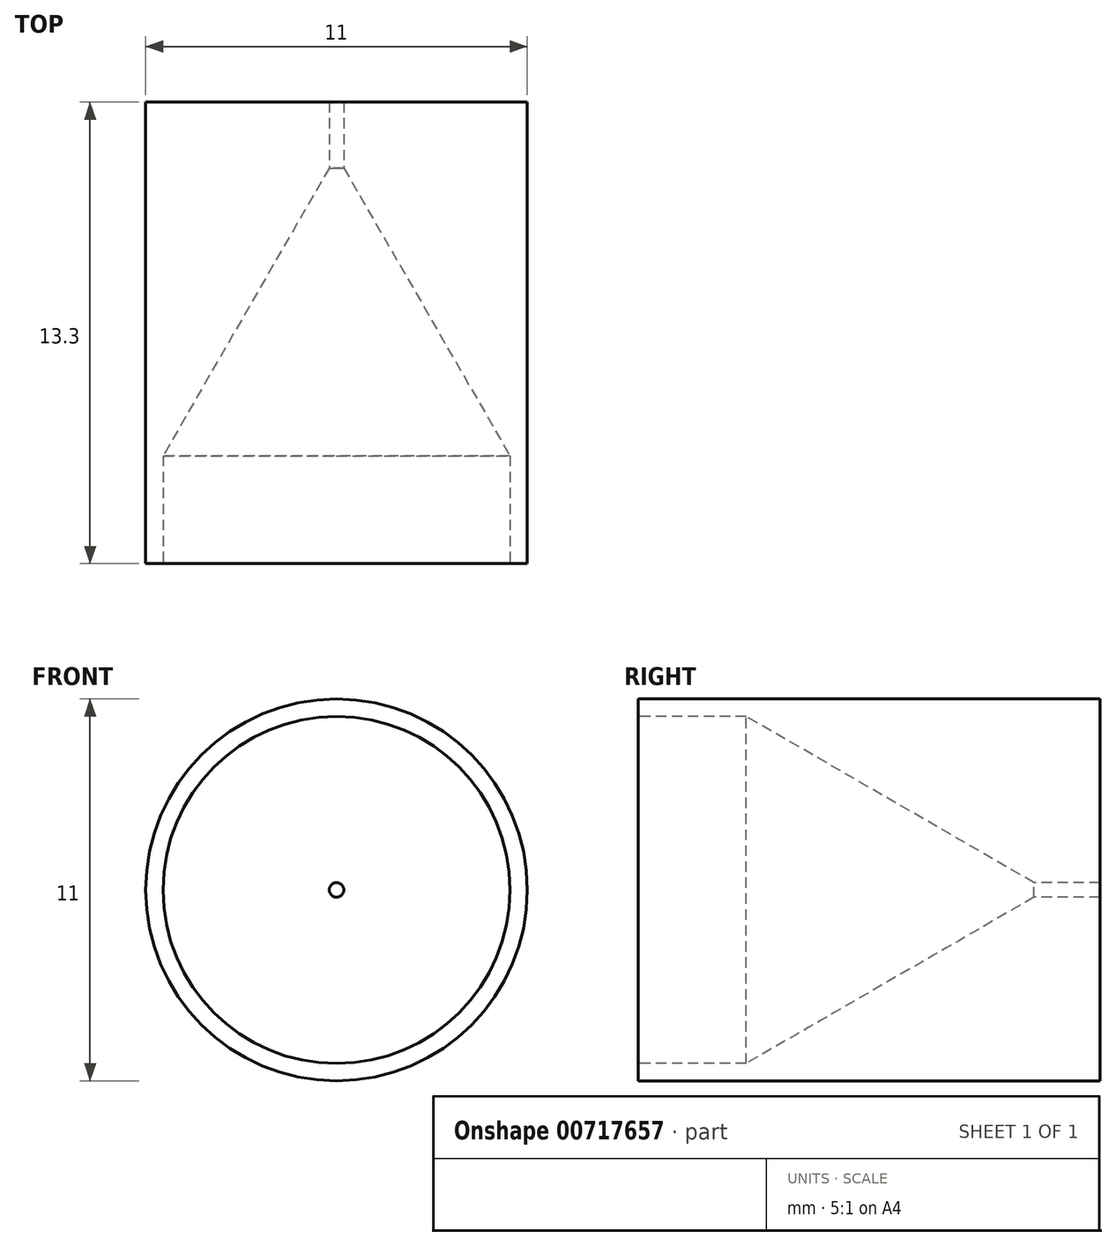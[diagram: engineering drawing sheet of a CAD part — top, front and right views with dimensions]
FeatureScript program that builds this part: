
annotation { "Feature Type Name" : "Feature", "Feature Type Description" : "" }
export const myFeature = defineFeature(function(context is Context, id is Id, definition is map)
    precondition{}
    {
        {
            var Q0;
            Q0=qCreatedBy(makeId("Front.planeOp"),FACE);
            var sketch = newSketch(context, id + "F0", { "sketchPlane" : qUnion([Q0])});
            skCircle(sketch, "E0", {"center": v(0, 0) * mm, "radius": 5.5 * mm});
            skSolve(sketch);
        }
        {
            var Q0;
            Q0 = qSketchRegion(id + "F0", true);
            extrude(context, id + "F1", {"entities" : qUnion([Q0]), "oppositeDirection" : true, "depth" : 11.9 * mm, "offsetDistance" : 25 * mm});
        }
        {
            var Q0;
            Q0=makeQuery(id+"F1.opExtrude","CAP_EDGE",EDGE,{"disambiguationData":[OSD([sQuery(id+"F0.wireOp",EDGE,"E0")])],"isStart":false});
            chamfer(context, id + "F2", {"entities" : qUnion([Q0]), "chamferType" : ChamferType.OFFSET_ANGLE, "width" : 5 * mm, "oppositeDirection" : true, "angle" : 60 * degree, "tangentPropagation" : true});
        }
        {
            var Q0;
            Q0=makeQuery(id+"F1.opExtrude","CAP_FACE",FACE,{"disambiguationData":[OSD([sQuery(id+"F0.wireOp",EDGE,"E0")])],"isStart":true});
            shell(context, id + "F3", {"entities" : qUnion([Q0]), "thickness" : .5 * mm});
        }
        {
            var Q0;
            Q0=qCreatedBy(makeId("Right.planeOp"),FACE);
            var sketch = newSketch(context, id + "F4", { "sketchPlane" : qUnion([Q0])});
            skLineSegment(sketch, "E1", {"start": v(0, 0) * mm, "end": v(30.47, 0) * mm, "construction": true});
            skLineSegment(sketch, "E2", {"start": v(3.24, -5.5) * mm, "end": v(11.9, -5.5) * mm});
            skLineSegment(sketch, "E3", {"start": v(3.24, 5.5) * mm, "end": v(11.9, 0.5) * mm});
            skLineSegment(sketch, "E4", {"start": v(11.9, -0.5) * mm, "end": v(3.24, -5.5) * mm});
            skLineSegment(sketch, "E5", {"start": v(11.9, -0.5) * mm, "end": v(11.9, -5.5) * mm});
            skSolve(sketch);
        }
        {
            var Q0;
            Q0 = qSketchRegion(id + "F4", true);
            var Q1;
            Q1=sQuery(id+"F4.wireOp",EDGE,"E1");
            revolve(context, id + "F5", {"operationType" : NewBodyOperationType.ADD, "surfaceOperationType" : NewSurfaceOperationType.NEW, "entities" : qUnion([Q0]), "axis" : qUnion([Q1]), "revolveType" : RevolveType.FULL});
        }
        {
            var Q0;
            {var subQ0=sQuery(id+"F0.wireOp",EDGE,"E0");Q0=makeQuery(id+"F3.opShell","OFFSET_FACE",FACE,{"disambiguationData":[OSD([subQ0]),TDD([makeQuery(id+"F1.opExtrude","CAP_FACE",FACE,{"disambiguationData":[OSD([subQ0])],"isStart":false})])]});}
            extrude(context, id + "F6", {"entities" : qUnion([Q0]), "operationType" : NewBodyOperationType.REMOVE, "oppositeDirection" : true, "depth" : 8.1 * mm, "offsetDistance" : 25 * mm});
        }
        {
            var Q0;
            Q0=makeQuery(id+"F5.boolean.opBoolean","MERGE",FACE,{"derivedFrom":[makeQuery(id+"F1.opExtrude","CAP_FACE",FACE,{"disambiguationData":[OSD([sQuery(id+"F0.wireOp",EDGE,"E0")])],"isStart":false}),makeQuery(id+"F5.opRevolve","SWEPT_FACE",FACE,{"disambiguationData":[OSD([sQuery(id+"F4.wireOp",EDGE,"E5")])]})]});
            var sketch = newSketch(context, id + "F7", { "sketchPlane" : qUnion([Q0])});
            skCircle(sketch, "E6.0.0", {"center": v(0, 0) * mm, "radius": 5.5 * mm});
            skSolve(sketch);
        }
        {
            var Q0;
            Q0=makeQuery(id+"F7.imprint","IMPRINT",FACE,{"disambiguationData":[TD([[makeQuery(id+"F7.imprint","IMPRINT",EDGE,{"derivedFrom":sQuery(id+"F7.wireOp",EDGE,"E6.0.0")}),-1.0]])]});
            extrude(context, id + "F8", {"entities" : qUnion([Q0]), "operationType" : NewBodyOperationType.ADD, "depth" : 1.4 * mm, "offsetDistance" : 25 * mm});
        }
    });
